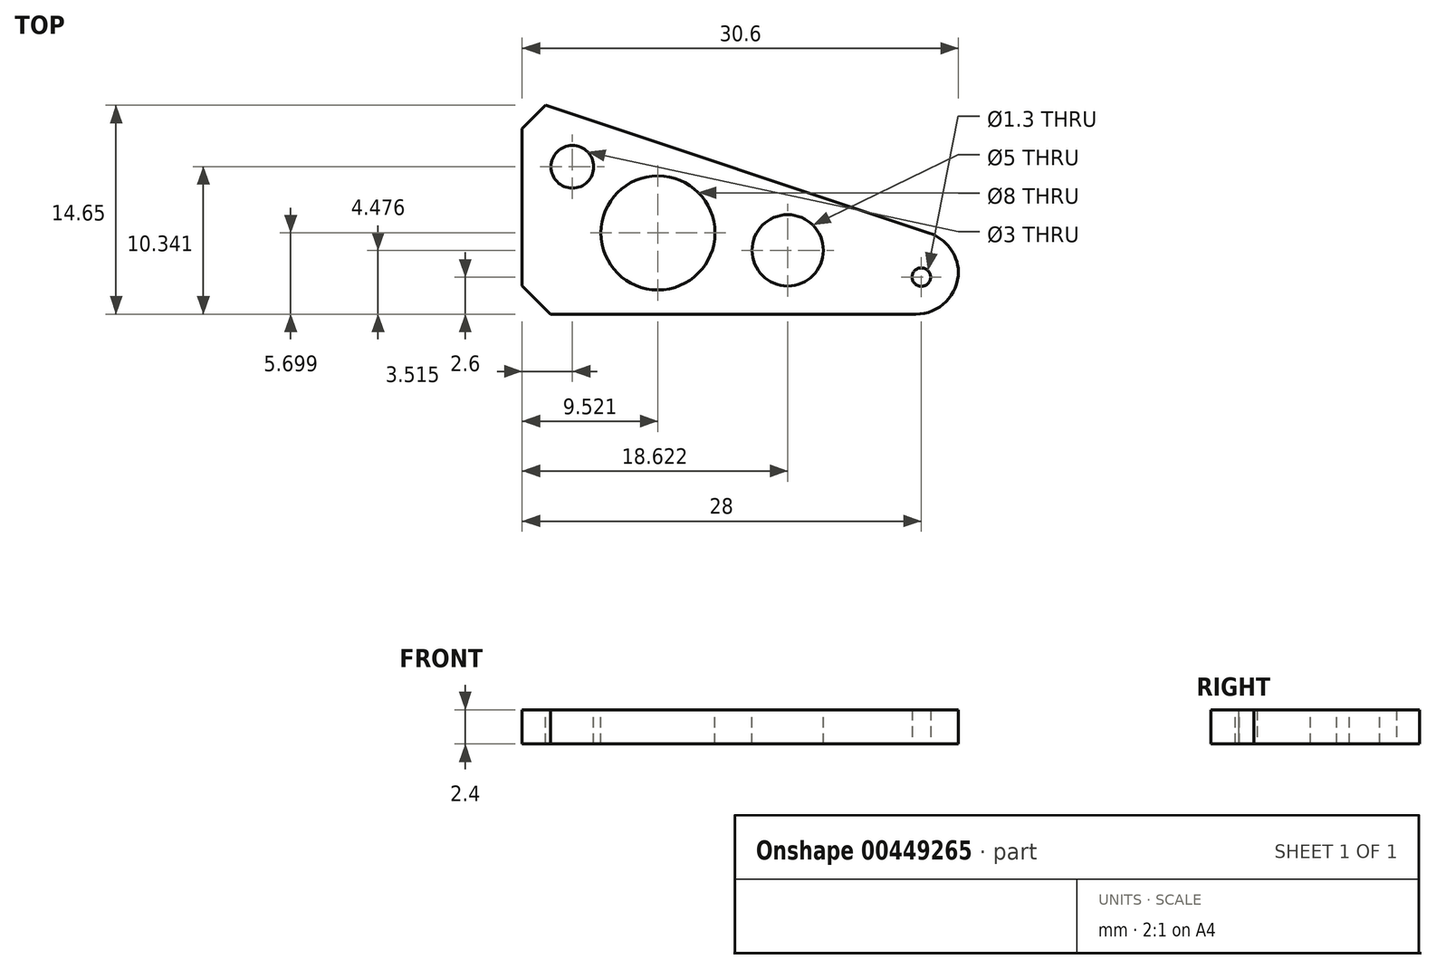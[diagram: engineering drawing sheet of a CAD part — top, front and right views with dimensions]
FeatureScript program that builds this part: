
annotation { "Feature Type Name" : "Feature", "Feature Type Description" : "" }
export const myFeature = defineFeature(function(context is Context, id is Id, definition is map)
    precondition{}
    {
        {
            var Q0;
            Q0=qCreatedBy(makeId("Top.planeOp"),FACE);
            var sketch = newSketch(context, id + "F0", { "sketchPlane" : qUnion([Q0])});
            skLineSegment(sketch, "E0.bottom", {"start": v(0, 0) * mm, "end": v(30.6, 0) * mm});
            skLineSegment(sketch, "E0.top", {"start": v(0, 15) * mm, "end": v(30.6, 15) * mm});
            skLineSegment(sketch, "E0.left", {"start": v(0, 0) * mm, "end": v(0, 15) * mm});
            skLineSegment(sketch, "E0.right", {"start": v(30.6, 0) * mm, "end": v(30.6, 15) * mm});
            skCircle(sketch, "E1", {"center": v(28, 2.6) * mm, "radius": 0.65 * mm});
            skSolve(sketch);
        }
        {
            var Q0;
            Q0=makeQuery(id+"F0.imprint","IMPRINT",FACE,{"disambiguationData":[TD([[makeQuery(id+"F0.imprint","IMPRINT",EDGE,{"derivedFrom":sQuery(id+"F0.wireOp",EDGE,"E0.bottom")}),1.0]])]});
            extrude(context, id + "F1", {"entities" : qUnion([Q0]), "depth" : 2.4 * mm});
        }
        {
            var Q0;
            Q0=makeQuery(id+"F1.opExtrude","SWEPT_EDGE",EDGE,{"disambiguationData":[OSD([sQuery(id+"F0.wireOp",EDGE,"E0.bottom"),sQuery(id+"F0.wireOp",EDGE,"E0.right")])]});
            fillet(context, id + "F2", {"entities" : qUnion([Q0]), "radius" : 3 * mm, "tangentPropagation" : true, "allowEdgeOverflow" : false});
        }
        {
            var Q0;
            Q0=makeQuery(id+"F1.opExtrude","SWEPT_EDGE",EDGE,{"disambiguationData":[OSD([sQuery(id+"F0.wireOp",EDGE,"E0.bottom"),sQuery(id+"F0.wireOp",EDGE,"E0.left")])]});
            var Q1;
            Q1=makeQuery(id+"F1.opExtrude","SWEPT_EDGE",EDGE,{"disambiguationData":[OSD([sQuery(id+"F0.wireOp",EDGE,"E0.top"),sQuery(id+"F0.wireOp",EDGE,"E0.left")])]});
            chamfer(context, id + "F3", {"entities" : qUnion([Q0, Q1]), "width" : 2 * mm, "tangentPropagation" : true});
        }
        {
            var Q0;
            Q0=makeQuery(id+"F1.opExtrude","SWEPT_EDGE",EDGE,{"disambiguationData":[OSD([sQuery(id+"F0.wireOp",EDGE,"E0.top"),sQuery(id+"F0.wireOp",EDGE,"E0.right")])]});
            chamfer(context, id + "F4", {"entities" : qUnion([Q0]), "chamferType" : ChamferType.TWO_OFFSETS, "width1" : 30 * mm, "oppositeDirection" : false, "width2" : 10 * mm, "tangentPropagation" : true});
        }
        {
            var Q0;
            {var subQ0=sQuery(id+"F0.wireOp",EDGE,"E0.right");Q0=makeQuery(id+"F4.opChamfer","BLEND_EDGE",EDGE,{"blendedFrom":[makeQuery(id+"F1.opExtrude","SWEPT_EDGE",EDGE,{"disambiguationData":[OSD([sQuery(id+"F0.wireOp",EDGE,"E0.top"),subQ0])]}),makeQuery(id+"F1.opExtrude","SWEPT_FACE",FACE,{"disambiguationData":[OSD([subQ0])]})],"blendedInto":[makeQuery(id+"F1.opExtrude","SWEPT_FACE",FACE,{"disambiguationData":[OSD([subQ0])]})]});}
            fillet(context, id + "F5", {"entities" : qUnion([Q0]), "radius" : 3 * mm, "tangentPropagation" : true, "allowEdgeOverflow" : false});
        }
        {
            var Q0;
            Q0=makeQuery(id+"F1.opExtrude","CAP_FACE",FACE,{"disambiguationData":[OSD([sQuery(id+"F0.wireOp",EDGE,"E0.bottom"),sQuery(id+"F0.wireOp",EDGE,"E0.top"),sQuery(id+"F0.wireOp",EDGE,"E0.left"),sQuery(id+"F0.wireOp",EDGE,"E0.right"),sQuery(id+"F0.wireOp",EDGE,"E1")])],"isStart":false});
            var sketch = newSketch(context, id + "F6", { "sketchPlane" : qUnion([Q0])});
            skCircle(sketch, "E2", {"center": v(3.51, 10.34) * mm, "radius": 1.5 * mm});
            skCircle(sketch, "E3", {"center": v(9.52, 5.7) * mm, "radius": 4 * mm});
            skCircle(sketch, "E4", {"center": v(18.62, 4.48) * mm, "radius": 2.5 * mm});
            skSolve(sketch);
        }
        {
            var Q0;
            Q0=makeQuery(id+"F6.imprint","IMPRINT",FACE,{"disambiguationData":[TD([[makeQuery(id+"F6.imprint","IMPRINT",EDGE,{"derivedFrom":sQuery(id+"F6.wireOp",EDGE,"E2")}),1.0]])]});
            var Q1;
            Q1=makeQuery(id+"F6.imprint","IMPRINT",FACE,{"disambiguationData":[TD([[makeQuery(id+"F6.imprint","IMPRINT",EDGE,{"derivedFrom":sQuery(id+"F6.wireOp",EDGE,"E3")}),1.0]])]});
            var Q2;
            Q2=makeQuery(id+"F6.imprint","IMPRINT",FACE,{"disambiguationData":[TD([[makeQuery(id+"F6.imprint","IMPRINT",EDGE,{"derivedFrom":sQuery(id+"F6.wireOp",EDGE,"E4")}),1.0]])]});
            extrude(context, id + "F7", {"entities" : qUnion([Q0, Q1, Q2]), "operationType" : NewBodyOperationType.REMOVE, "oppositeDirection" : true, "depth" : 25 * mm});
        }
    });
